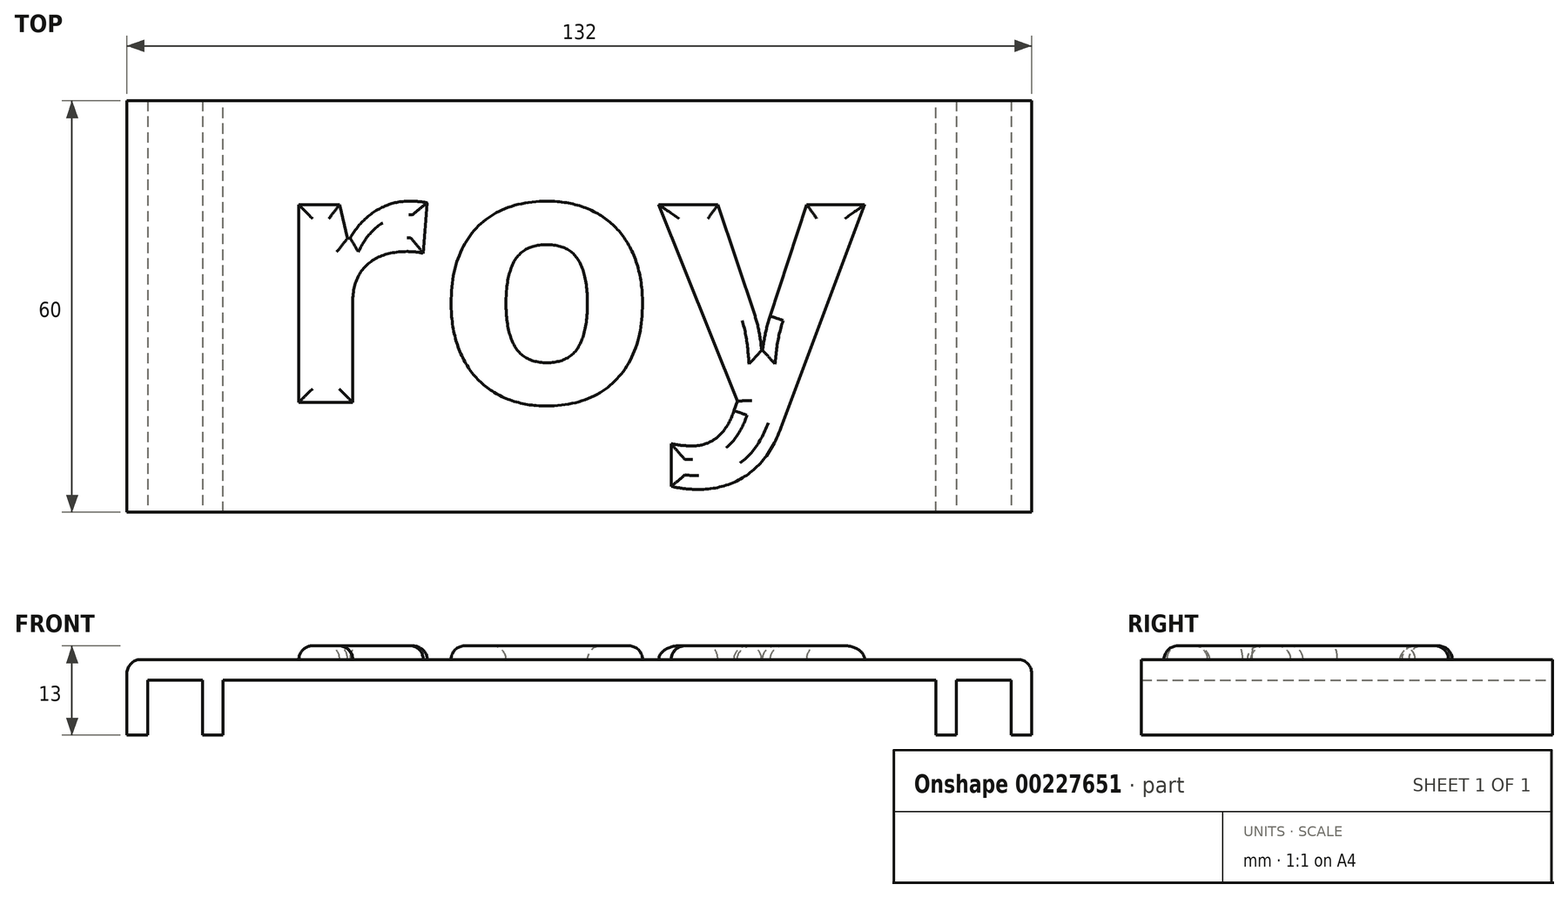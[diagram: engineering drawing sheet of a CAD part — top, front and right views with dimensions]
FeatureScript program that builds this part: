
annotation { "Feature Type Name" : "Feature", "Feature Type Description" : "" }
export const myFeature = defineFeature(function(context is Context, id is Id, definition is map)
    precondition{}
    {
        {
            var Q0;
            Q0=qCreatedBy(makeId("Top.planeOp"),FACE);
            var sketch = newSketch(context, id + "F0", { "sketchPlane" : qUnion([Q0])});
            skLineSegment(sketch, "E0.bottom", {"start": v(52, -30) * mm, "end": v(-52, -30) * mm});
            skLineSegment(sketch, "E0.top", {"start": v(52, 30) * mm, "end": v(-52, 30) * mm});
            skLineSegment(sketch, "E0.left", {"start": v(52, -30) * mm, "end": v(52, 30) * mm});
            skLineSegment(sketch, "E0.right", {"start": v(-52, -30) * mm, "end": v(-52, 30) * mm});
            skPoint(sketch, "E0.middle", {"position": v(0, 0) * mm});
            skLineSegment(sketch, "E1", {"start": v(-52, 30) * mm, "end": v(-55, 30) * mm});
            skLineSegment(sketch, "E2", {"start": v(-55, 30) * mm, "end": v(-55, -30) * mm});
            skLineSegment(sketch, "E3", {"start": v(-55, -30) * mm, "end": v(-52, -30) * mm});
            skLineSegment(sketch, "E4", {"start": v(52, 30) * mm, "end": v(55, 30) * mm});
            skLineSegment(sketch, "E5", {"start": v(55, 30) * mm, "end": v(55, -30) * mm});
            skLineSegment(sketch, "E6", {"start": v(55, -30) * mm, "end": v(52, -30) * mm});
            skLineSegment(sketch, "E7", {"start": v(-55, 30) * mm, "end": v(-63, 30) * mm});
            skLineSegment(sketch, "E8", {"start": v(-63, 30) * mm, "end": v(-63, -30) * mm});
            skLineSegment(sketch, "E9", {"start": v(-63, -30) * mm, "end": v(-55, -30) * mm});
            skLineSegment(sketch, "E10", {"start": v(-63, 30) * mm, "end": v(-66, 30) * mm});
            skLineSegment(sketch, "E11", {"start": v(-66, 30) * mm, "end": v(-66, -30) * mm});
            skLineSegment(sketch, "E12", {"start": v(-66, -30) * mm, "end": v(-63, -30) * mm});
            skLineSegment(sketch, "E13", {"start": v(55, 30) * mm, "end": v(63, 30) * mm});
            skLineSegment(sketch, "E14", {"start": v(63, 30) * mm, "end": v(63, -30) * mm});
            skLineSegment(sketch, "E15", {"start": v(63, -30) * mm, "end": v(55, -30) * mm});
            skLineSegment(sketch, "E16", {"start": v(63, 30) * mm, "end": v(66, 30) * mm});
            skLineSegment(sketch, "E17", {"start": v(66, 30) * mm, "end": v(66, -30) * mm});
            skLineSegment(sketch, "E18", {"start": v(66, -30) * mm, "end": v(63, -30) * mm});
            skSolve(sketch);
        }
        {
            var Q0;
            Q0=makeQuery(id+"F0.imprint","IMPRINT",FACE,{"disambiguationData":[TD([[makeQuery(id+"F0.imprint","IMPRINT",EDGE,{"derivedFrom":sQuery(id+"F0.wireOp",EDGE,"E8")}),-1.0]])]});
            var Q1;
            Q1=makeQuery(id+"F0.imprint","IMPRINT",FACE,{"disambiguationData":[TD([[makeQuery(id+"F0.imprint","IMPRINT",EDGE,{"derivedFrom":sQuery(id+"F0.wireOp",EDGE,"E0.right")}),1.0]])]});
            var Q2;
            Q2=makeQuery(id+"F0.imprint","IMPRINT",FACE,{"disambiguationData":[TD([[makeQuery(id+"F0.imprint","IMPRINT",EDGE,{"derivedFrom":sQuery(id+"F0.wireOp",EDGE,"E0.left")}),-1.0]])]});
            var Q3;
            Q3=makeQuery(id+"F0.imprint","IMPRINT",FACE,{"disambiguationData":[TD([[makeQuery(id+"F0.imprint","IMPRINT",EDGE,{"derivedFrom":sQuery(id+"F0.wireOp",EDGE,"E14")}),1.0]])]});
            extrude(context, id + "F1", {"entities" : qUnion([Q0, Q1, Q2, Q3]), "oppositeDirection" : true, "depth" : 11 * mm});
        }
        {
            var Q0;
            Q0=makeQuery(id+"F0.imprint","IMPRINT",FACE,{"disambiguationData":[TD([[makeQuery(id+"F0.imprint","IMPRINT",EDGE,{"derivedFrom":sQuery(id+"F0.wireOp",EDGE,"E2")}),-1.0]])]});
            var Q1;
            Q1=makeQuery(id+"F0.imprint","IMPRINT",FACE,{"disambiguationData":[TD([[makeQuery(id+"F0.imprint","IMPRINT",EDGE,{"derivedFrom":sQuery(id+"F0.wireOp",EDGE,"E5")}),1.0]])]});
            var Q2;
            Q2=makeQuery(id+"F0.imprint","IMPRINT",FACE,{"disambiguationData":[TD([[makeQuery(id+"F0.imprint","IMPRINT",EDGE,{"derivedFrom":sQuery(id+"F0.wireOp",EDGE,"E0.bottom")}),-1.0]])]});
            extrude(context, id + "F2", {"entities" : qUnion([Q0, Q1, Q2]), "operationType" : NewBodyOperationType.ADD, "oppositeDirection" : true, "depth" : 3 * mm});
        }
        {
            var Q0;
            Q0=makeQuery(id+"F0.imprint","IMPRINT",FACE,{"disambiguationData":[TD([[makeQuery(id+"F0.imprint","IMPRINT",EDGE,{"derivedFrom":sQuery(id+"F0.wireOp",EDGE,"E0.bottom")}),-1.0]])]});
            var sketch = newSketch(context, id + "F3", { "sketchPlane" : qUnion([Q0])});
            skText(sketch, "E19", { "text": "roy", "fontName": "OpenSans-Bold.ttf"});
            const initialGuessF3  = {"E19": [-0.04505, -0.014, 1, 0, 0.038]};
            skSetInitialGuess(sketch, initialGuessF3);
            skSolve(sketch);
        }
        {
            var Q0;
            Q0=makeQuery(id+"F3.imprint","IMPRINT",FACE,{"disambiguationData":[TD([[makeQuery(id+"F3.imprint","IMPRINT",EDGE,{"derivedFrom":sQuery(id+"F3.wireOp",EDGE,"E19.sketch_text.stroke-0")}),-1.0]])]});
            var Q1;
            Q1=makeQuery(id+"F3.imprint","IMPRINT",FACE,{"disambiguationData":[TD([[makeQuery(id+"F3.imprint","IMPRINT",EDGE,{"derivedFrom":sQuery(id+"F3.wireOp",EDGE,"E19.sketch_text.stroke-13")}),-1.0]])]});
            var Q2;
            Q2=makeQuery(id+"F3.imprint","IMPRINT",FACE,{"disambiguationData":[TD([[makeQuery(id+"F3.imprint","IMPRINT",EDGE,{"derivedFrom":sQuery(id+"F3.wireOp",EDGE,"E19.sketch_text.stroke-31")}),-1.0]])]});
            extrude(context, id + "F4", {"entities" : qUnion([Q0, Q1, Q2]), "operationType" : NewBodyOperationType.ADD, "depth" : 2 * mm});
        }
        {
            var Q0;
            Q0=makeQuery(id+"F1.opExtrude","CAP_EDGE",EDGE,{"disambiguationData":[OSD([sQuery(id+"F0.wireOp",EDGE,"E11")])],"isStart":true});
            var Q1;
            Q1=makeQuery(id+"F1.opExtrude","CAP_EDGE",EDGE,{"disambiguationData":[OSD([sQuery(id+"F0.wireOp",EDGE,"E17")])],"isStart":true});
            fillet(context, id + "F5", {"entities" : qUnion([Q0, Q1]), "radius" : 2 * mm, "tangentPropagation" : true, "allowEdgeOverflow" : false});
        }
        {
            var Q0;
            Q0=makeQuery(id+"F4.opExtrude","CAP_EDGE",EDGE,{"disambiguationData":[OSD([sQuery(id+"F3.wireOp",EDGE,"E19.sketch_text.stroke-23")])],"isStart":false});
            var Q1;
            Q1=makeQuery(id+"F4.opExtrude","CAP_EDGE",EDGE,{"disambiguationData":[OSD([sQuery(id+"F3.wireOp",EDGE,"E19.sketch_text.stroke-13")])],"isStart":false});
            var Q2;
            Q2=makeQuery(id+"F4.opExtrude","CAP_EDGE",EDGE,{"disambiguationData":[OSD([sQuery(id+"F3.wireOp",EDGE,"E19.sketch_text.stroke-47")])],"isStart":false});
            var Q3;
            Q3=makeQuery(id+"F4.opExtrude","CAP_EDGE",EDGE,{"disambiguationData":[OSD([sQuery(id+"F3.wireOp",EDGE,"E19.sketch_text.stroke-32")])],"isStart":false});
            var Q4;
            Q4=makeQuery(id+"F4.opExtrude","CAP_EDGE",EDGE,{"disambiguationData":[OSD([sQuery(id+"F3.wireOp",EDGE,"E19.sketch_text.stroke-31")])],"isStart":false});
            var Q5;
            Q5=makeQuery(id+"F4.opExtrude","CAP_EDGE",EDGE,{"disambiguationData":[OSD([sQuery(id+"F3.wireOp",EDGE,"E19.sketch_text.stroke-37")])],"isStart":false});
            var Q6;
            Q6=makeQuery(id+"F4.opExtrude","CAP_EDGE",EDGE,{"disambiguationData":[OSD([sQuery(id+"F3.wireOp",EDGE,"E19.sketch_text.stroke-42")])],"isStart":false});
            var Q7;
            Q7=makeQuery(id+"F4.opExtrude","CAP_EDGE",EDGE,{"disambiguationData":[OSD([sQuery(id+"F3.wireOp",EDGE,"E19.sketch_text.stroke-41")])],"isStart":false});
            var Q8;
            Q8=makeQuery(id+"F4.opExtrude","CAP_EDGE",EDGE,{"disambiguationData":[OSD([sQuery(id+"F3.wireOp",EDGE,"E19.sketch_text.stroke-43")])],"isStart":false});
            var Q9;
            Q9=makeQuery(id+"F4.opExtrude","CAP_EDGE",EDGE,{"disambiguationData":[OSD([sQuery(id+"F3.wireOp",EDGE,"E19.sketch_text.stroke-7")])],"isStart":false});
            var Q10;
            Q10=makeQuery(id+"F4.opExtrude","CAP_EDGE",EDGE,{"disambiguationData":[OSD([sQuery(id+"F3.wireOp",EDGE,"E19.sketch_text.stroke-6")])],"isStart":false});
            var Q11;
            Q11=makeQuery(id+"F4.opExtrude","CAP_EDGE",EDGE,{"disambiguationData":[OSD([sQuery(id+"F3.wireOp",EDGE,"E19.sketch_text.stroke-5")])],"isStart":false});
            var Q12;
            Q12=makeQuery(id+"F4.opExtrude","CAP_EDGE",EDGE,{"disambiguationData":[OSD([sQuery(id+"F3.wireOp",EDGE,"E19.sketch_text.stroke-1")])],"isStart":false});
            var Q13;
            Q13=makeQuery(id+"F4.opExtrude","CAP_EDGE",EDGE,{"disambiguationData":[OSD([sQuery(id+"F3.wireOp",EDGE,"E19.sketch_text.stroke-0")])],"isStart":false});
            var Q14;
            Q14=makeQuery(id+"F4.opExtrude","CAP_EDGE",EDGE,{"disambiguationData":[OSD([sQuery(id+"F3.wireOp",EDGE,"E19.sketch_text.stroke-8")])],"isStart":false});
            var Q15;
            Q15=makeQuery(id+"F4.opExtrude","CAP_EDGE",EDGE,{"disambiguationData":[OSD([sQuery(id+"F3.wireOp",EDGE,"E19.sketch_text.stroke-9")])],"isStart":false});
            var Q16;
            Q16=makeQuery(id+"F4.opExtrude","CAP_EDGE",EDGE,{"disambiguationData":[OSD([sQuery(id+"F3.wireOp",EDGE,"E19.sketch_text.stroke-10")])],"isStart":false});
            var Q17;
            Q17=makeQuery(id+"F4.opExtrude","CAP_EDGE",EDGE,{"disambiguationData":[OSD([sQuery(id+"F3.wireOp",EDGE,"E19.sketch_text.stroke-33")])],"isStart":false});
            var Q18;
            Q18=makeQuery(id+"F4.opExtrude","CAP_EDGE",EDGE,{"disambiguationData":[OSD([sQuery(id+"F3.wireOp",EDGE,"E19.sketch_text.stroke-34")])],"isStart":false});
            var Q19;
            Q19=makeQuery(id+"F4.opExtrude","CAP_EDGE",EDGE,{"disambiguationData":[OSD([sQuery(id+"F3.wireOp",EDGE,"E19.sketch_text.stroke-35")])],"isStart":false});
            fillet(context, id + "F6", {"entities" : qUnion([Q0, Q1, Q2, Q3, Q4, Q5, Q6, Q7, Q8, Q9, Q10, Q11, Q12, Q13, Q14, Q15, Q16, Q17, Q18, Q19]), "radius" : 2 * mm, "tangentPropagation" : true, "allowEdgeOverflow" : false});
        }
    });
